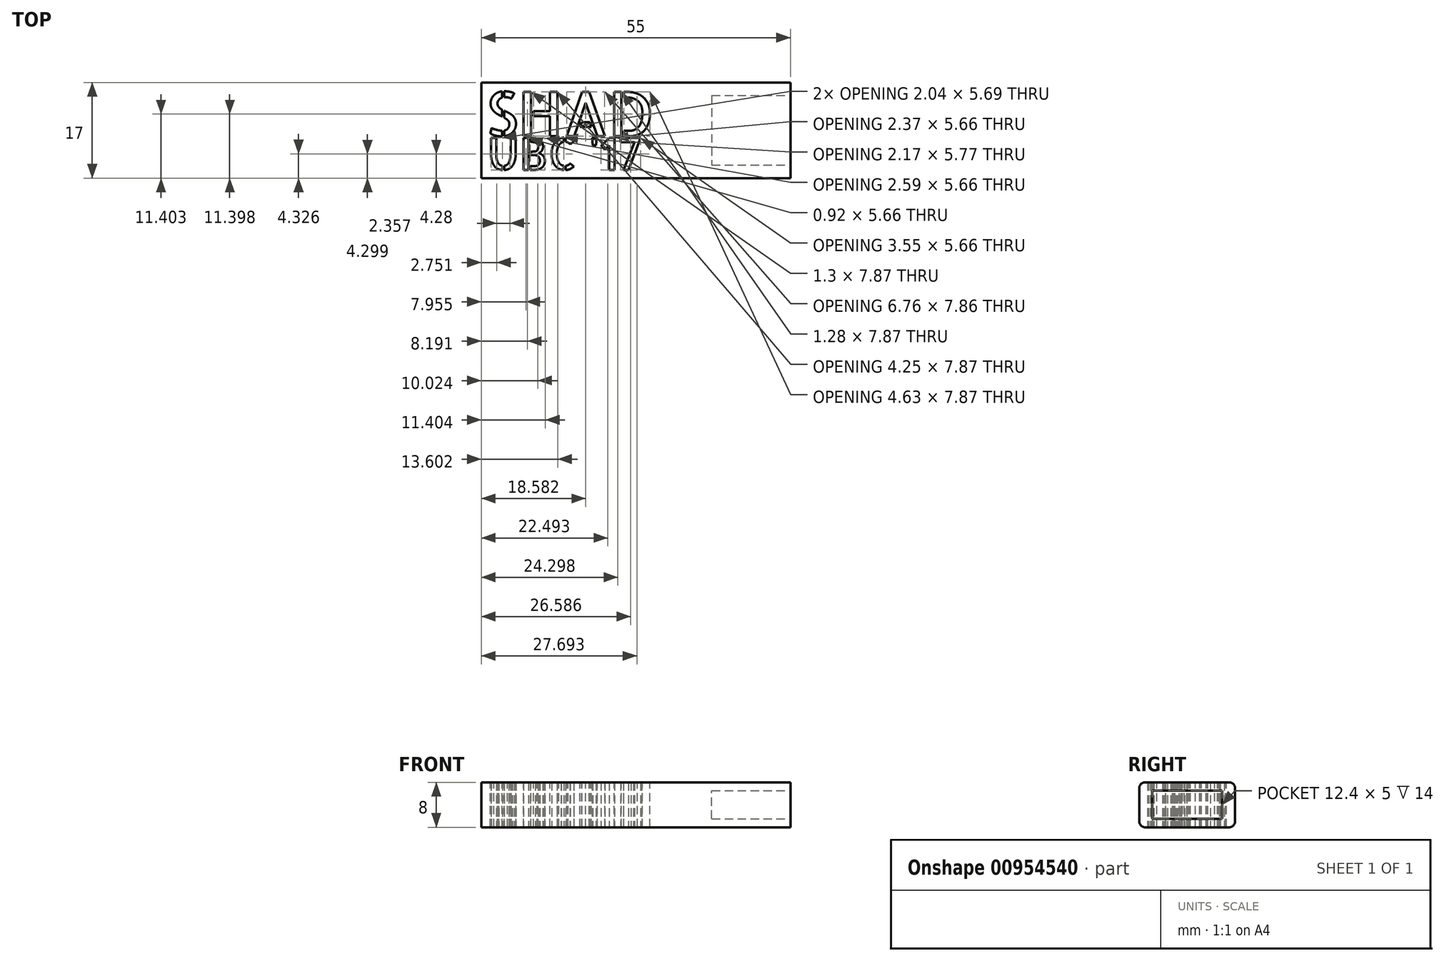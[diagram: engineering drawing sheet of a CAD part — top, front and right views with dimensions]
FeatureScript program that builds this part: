
annotation { "Feature Type Name" : "Feature", "Feature Type Description" : "" }
export const myFeature = defineFeature(function(context is Context, id is Id, definition is map)
    precondition{}
    {
        {
            var Q0;
            Q0=qCreatedBy(makeId("Front.planeOp"),FACE);
            var sketch = newSketch(context, id + "F0", { "sketchPlane" : qUnion([Q0])});
            skLineSegment(sketch, "E0.bottom", {"start": v(7.5, -4) * mm, "end": v(-7.5, -4) * mm});
            skLineSegment(sketch, "E0.top", {"start": v(7.5, 4) * mm, "end": v(-7.5, 4) * mm});
            skLineSegment(sketch, "E0.left", {"start": v(8.5, -3) * mm, "end": v(8.5, 3) * mm});
            skLineSegment(sketch, "E0.right", {"start": v(-8.5, -3) * mm, "end": v(-8.5, 3) * mm});
            skPoint(sketch, "E0.middle", {"position": v(0, 0) * mm});
            skPoint(sketch, "E1.visualSharp", {"position": v(-8.5, 4) * mm});
            skArc(sketch, "E1.filletArc", {"start": v(-7.5, 4) * mm, "mid": v(-8.2, 3.7) * mm, "end": v(-8.5, 3) * mm});
            skPoint(sketch, "E2.visualSharp", {"position": v(-8.5, -4) * mm});
            skArc(sketch, "E2.filletArc", {"start": v(-8.5, -3) * mm, "mid": v(-8.2, -3.7) * mm, "end": v(-7.5, -4) * mm});
            skPoint(sketch, "E3.visualSharp", {"position": v(8.5, -4) * mm});
            skArc(sketch, "E3.filletArc", {"start": v(7.5, -4) * mm, "mid": v(8.2, -3.7) * mm, "end": v(8.5, -3) * mm});
            skPoint(sketch, "E4.visualSharp", {"position": v(8.5, 4) * mm});
            skArc(sketch, "E4.filletArc", {"start": v(8.5, 3) * mm, "mid": v(8.2, 3.7) * mm, "end": v(7.5, 4) * mm});
            skSolve(sketch);
        }
        {
            var Q0;
            Q0 = qSketchRegion(id + "F0", true);
            extrude(context, id + "F1", {"entities" : qUnion([Q0]), "depth" : 55 * mm, "offsetDistance" : 25 * mm});
        }
        {
            var Q0;
            Q0=makeQuery(id+"F1.opExtrude","CAP_FACE",FACE,{"disambiguationData":[OSD([sQuery(id+"F0.wireOp",EDGE,"E0.bottom"),sQuery(id+"F0.wireOp",EDGE,"E0.top"),sQuery(id+"F0.wireOp",EDGE,"E0.left"),sQuery(id+"F0.wireOp",EDGE,"E0.right"),sQuery(id+"F0.wireOp",EDGE,"E1.filletArc"),sQuery(id+"F0.wireOp",EDGE,"E2.filletArc"),sQuery(id+"F0.wireOp",EDGE,"E3.filletArc"),sQuery(id+"F0.wireOp",EDGE,"E4.filletArc")])],"isStart":false});
            var sketch = newSketch(context, id + "F2", { "sketchPlane" : qUnion([Q0])});
            skLineSegment(sketch, "E5.bottom", {"start": v(6.2, -2.5) * mm, "end": v(-6.2, -2.5) * mm});
            skLineSegment(sketch, "E5.top", {"start": v(6.2, 2.5) * mm, "end": v(-6.2, 2.5) * mm});
            skLineSegment(sketch, "E5.left", {"start": v(6.2, -2.5) * mm, "end": v(6.2, 2.5) * mm});
            skLineSegment(sketch, "E5.right", {"start": v(-6.2, -2.5) * mm, "end": v(-6.2, 2.5) * mm});
            skPoint(sketch, "E5.middle", {"position": v(0, 0) * mm});
            skSolve(sketch);
        }
        {
            var Q0;
            Q0=makeQuery(id+"F2.imprint","IMPRINT",FACE,{"disambiguationData":[TD([[makeQuery(id+"F2.imprint","IMPRINT",EDGE,{"derivedFrom":sQuery(id+"F2.wireOp",EDGE,"E5.bottom")}),-1.0]])]});
            extrude(context, id + "F3", {"entities" : qUnion([Q0]), "operationType" : NewBodyOperationType.REMOVE, "oppositeDirection" : true, "depth" : 14 * mm, "offsetDistance" : 25 * mm});
        }
        {
            var Q0;
            Q0=makeQuery(id+"F1.opExtrude","SWEPT_BODY",BODY,{"disambiguationData":[OSD([sQuery(id+"F0.wireOp",EDGE,"E0.bottom"),sQuery(id+"F0.wireOp",EDGE,"E0.top"),sQuery(id+"F0.wireOp",EDGE,"E0.left"),sQuery(id+"F0.wireOp",EDGE,"E0.right"),sQuery(id+"F0.wireOp",EDGE,"E1.filletArc"),sQuery(id+"F0.wireOp",EDGE,"E2.filletArc"),sQuery(id+"F0.wireOp",EDGE,"E3.filletArc"),sQuery(id+"F0.wireOp",EDGE,"E4.filletArc")])]});
            var Q1;
            Q1=makeQuery(id+"F1.opExtrude","CAP_EDGE",EDGE,{"disambiguationData":[OSD([sQuery(id+"F0.wireOp",EDGE,"E0.left")])],"isStart":true});
            transform(context, id + "F4", {"entities" : qUnion([Q0]), "transformType" : TransformType.ROTATION, "transformAxis" : qUnion([Q1]), "angle" : 90 * degree, "makeCopy" : false});
        }
        {
            var Q0;
            Q0=qCreatedBy(makeId("Top.planeOp"),FACE);
            var sketch = newSketch(context, id + "F5", { "sketchPlane" : qUnion([Q0])});
            skText(sketch, "E6", { "text": "SHAD", "fontName": "AllertaStencil-Regular.ttf"});
            const initialGuessF5  = {"E6": [0.00925, -0.00953, 1, 0, 0.00787]};
            skSetInitialGuess(sketch, initialGuessF5);
            skSolve(sketch);
        }
        {
            var Q0;
            Q0=qCreatedBy(makeId("Top.planeOp"),FACE);
            var sketch = newSketch(context, id + "F6", { "sketchPlane" : qUnion([Q0])});
            skText(sketch, "E7", { "text": "UBC \'17", "fontName": "AllertaStencil-Regular.ttf"});
            const initialGuessF6  = {"E7": [0.0096, -0.01553, 1, 0, 0.00566]};
            skSetInitialGuess(sketch, initialGuessF6);
            skSolve(sketch);
        }
        {
            var Q0;
            Q0 = qSketchRegion(id + "F5", true);
            extrude(context, id + "F7", {"entities" : qUnion([Q0]), "operationType" : NewBodyOperationType.REMOVE, "oppositeDirection" : true, "depth" : 25 * mm, "offsetDistance" : 25 * mm, "hasSecondDirection" : true, "secondDirectionOppositeDirection" : false, "secondDirectionDepth" : 25 * mm});
        }
        {
            var Q0;
            Q0 = qSketchRegion(id + "F6", true);
            extrude(context, id + "F8", {"entities" : qUnion([Q0]), "operationType" : NewBodyOperationType.REMOVE, "depth" : 25 * mm, "offsetDistance" : 25 * mm, "hasSecondDirection" : true, "secondDirectionOppositeDirection" : true, "secondDirectionDepth" : 25 * mm});
        }
    });
